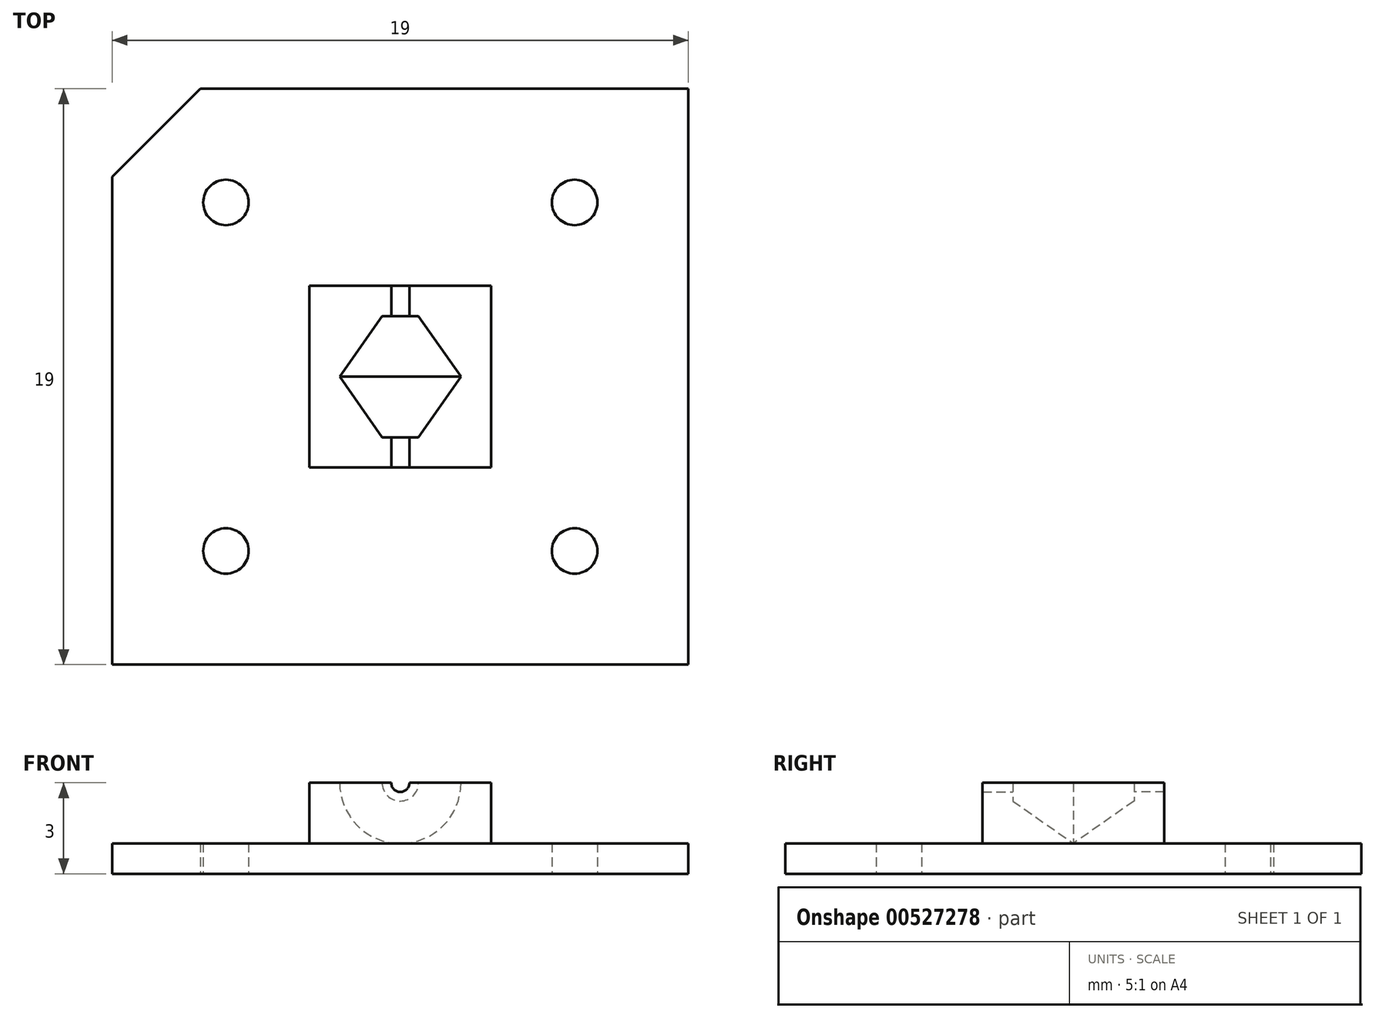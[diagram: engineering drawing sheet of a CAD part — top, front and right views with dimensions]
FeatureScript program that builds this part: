
annotation { "Feature Type Name" : "Feature", "Feature Type Description" : "" }
export const myFeature = defineFeature(function(context is Context, id is Id, definition is map)
    precondition{}
    {
        {
            var Q0;
            Q0=qCreatedBy(makeId("Top.planeOp"),FACE);
            var sketch = newSketch(context, id + "F0", { "sketchPlane" : qUnion([Q0])});
            skLineSegment(sketch, "E0.bottom", {"start": v(-2, 2) * mm, "end": v(2, 2) * mm});
            skLineSegment(sketch, "E0.top", {"start": v(-2, -2) * mm, "end": v(2, -2) * mm});
            skLineSegment(sketch, "E0.left", {"start": v(-2, 2) * mm, "end": v(-2, -2) * mm});
            skLineSegment(sketch, "E0.right", {"start": v(2, 2) * mm, "end": v(2, -2) * mm});
            skPoint(sketch, "E0.middle", {"position": v(0, 0) * mm});
            skLineSegment(sketch, "E1", {"start": v(0.6, 2) * mm, "end": v(2, 0) * mm});
            skLineSegment(sketch, "E2.MirrorCS", {"start": v(0.6, -2) * mm, "end": v(2, 0) * mm});
            skLineSegment(sketch, "E3.MirrorCS", {"start": v(-0.6, 2) * mm, "end": v(-2, 0) * mm});
            skLineSegment(sketch, "E4.MirrorCS", {"start": v(-0.6, -2) * mm, "end": v(-2, 0) * mm});
            skLineSegment(sketch, "E5", {"start": v(-0.6, -2) * mm, "end": v(-0.6, 2) * mm});
            skLineSegment(sketch, "E6.MirrorCS", {"start": v(0.6, -2) * mm, "end": v(0.6, 2) * mm});
            skLineSegment(sketch, "E7", {"start": v(0, 2) * mm, "end": v(0, -2) * mm});
            skCircle(sketch, "E8", {"center": v(-5.75, 5.75) * mm, "radius": 0.75 * mm});
            skCircle(sketch, "E9.MirrorC", {"center": v(5.75, 5.75) * mm, "radius": 0.75 * mm});
            skCircle(sketch, "E10.MirrorC", {"center": v(5.75, -5.75) * mm, "radius": 0.75 * mm});
            skCircle(sketch, "E11.MirrorC", {"center": v(-5.75, -5.75) * mm, "radius": 0.75 * mm});
            skLineSegment(sketch, "E12.bottom", {"start": v(-9.5, 9.5) * mm, "end": v(9.5, 9.5) * mm});
            skLineSegment(sketch, "E12.top", {"start": v(-9.5, -9.5) * mm, "end": v(9.5, -9.5) * mm});
            skLineSegment(sketch, "E12.left", {"start": v(-9.5, 9.5) * mm, "end": v(-9.5, -9.5) * mm});
            skLineSegment(sketch, "E12.right", {"start": v(9.5, 9.5) * mm, "end": v(9.5, -9.5) * mm});
            skLineSegment(sketch, "E13", {"start": v(0.3, 2) * mm, "end": v(0.3, -2) * mm});
            skLineSegment(sketch, "E14.MirrorCS", {"start": v(-0.3, 2) * mm, "end": v(-0.3, -2) * mm});
            skLineSegment(sketch, "E15", {"start": v(-6.6, 9.5) * mm, "end": v(-9.5, 6.6) * mm});
            skSolve(sketch);
        }
        {
            var Q0;
            Q0=qCreatedBy(makeId("Front.planeOp"),FACE);
            var sketch = newSketch(context, id + "F1", { "sketchPlane" : qUnion([Q0])});
            skLineSegment(sketch, "E16.bottom", {"start": v(0, 0) * mm, "end": v(2, 0) * mm});
            skLineSegment(sketch, "E16.top", {"start": v(0, 3) * mm, "end": v(2, 3) * mm});
            skLineSegment(sketch, "E16.left", {"start": v(0, 0) * mm, "end": v(0, 3) * mm});
            skLineSegment(sketch, "E16.right", {"start": v(2, 0) * mm, "end": v(2, 3) * mm});
            skCircle(sketch, "E17", {"center": v(0, 3) * mm, "radius": 0.6 * mm});
            skCircle(sketch, "E18", {"center": v(0, 3) * mm, "radius": 0.3 * mm});
            skLineSegment(sketch, "E19.bottom", {"start": v(0, 3) * mm, "end": v(-2, 3) * mm});
            skLineSegment(sketch, "E19.top", {"start": v(0, 0) * mm, "end": v(-2, 0) * mm});
            skLineSegment(sketch, "E19.left", {"start": v(0, 3) * mm, "end": v(0, 0) * mm});
            skLineSegment(sketch, "E19.right", {"start": v(-2, 3) * mm, "end": v(-2, 0) * mm});
            skLineSegment(sketch, "E20.top", {"start": v(0, 1) * mm, "end": v(2, 1) * mm});
            skLineSegment(sketch, "E20.left", {"start": v(0, 0) * mm, "end": v(0, 1) * mm});
            skLineSegment(sketch, "E21.MirrorCS", {"start": v(0, 1) * mm, "end": v(-2, 1) * mm});
            skSolve(sketch);
        }
        {
            var Q0;
            {var subQ3=sQuery(id+"F0.wireOp",EDGE,"E4.MirrorCS");Q0=makeQuery(id+"F0.imprint","IMPRINT",FACE,{"disambiguationData":[TD([[makeQuery(id+"F0.imprint","IMPRINT",EDGE,{"derivedFrom":subQ3}),1.0]])]});}
            var Q1;
            {var subQ3=sQuery(id+"F0.wireOp",EDGE,"E3.MirrorCS");Q1=makeQuery(id+"F0.imprint","IMPRINT",FACE,{"disambiguationData":[TD([[makeQuery(id+"F0.imprint","IMPRINT",EDGE,{"derivedFrom":subQ3}),-1.0]])]});}
            var Q2;
            {var subQ3=sQuery(id+"F0.wireOp",EDGE,"E1");Q2=makeQuery(id+"F0.imprint","IMPRINT",FACE,{"disambiguationData":[TD([[makeQuery(id+"F0.imprint","IMPRINT",EDGE,{"derivedFrom":subQ3}),1.0]])]});}
            var Q3;
            {var subQ3=sQuery(id+"F0.wireOp",EDGE,"E2.MirrorCS");Q3=makeQuery(id+"F0.imprint","IMPRINT",FACE,{"disambiguationData":[TD([[makeQuery(id+"F0.imprint","IMPRINT",EDGE,{"derivedFrom":subQ3}),-1.0]])]});}
            extrude(context, id + "F2", {"entities" : qUnion([Q0, Q1, Q2, Q3]), "depth" : 3 * mm, "offsetDistance" : 25 * mm});
        }
        {
            var Q0;
            Q0=makeQuery(id+"F0.imprint","IMPRINT",FACE,{"disambiguationData":[TD([[makeQuery(id+"F0.imprint","IMPRINT",EDGE,{"derivedFrom":sQuery(id+"F0.wireOp",EDGE,"E3.MirrorCS")}),1.0]])]});
            var Q1;
            {var subQ0=sQuery(id+"F0.wireOp",EDGE,"E5");Q1=makeQuery(id+"F0.imprint","IMPRINT",FACE,{"disambiguationData":[TD([[makeQuery(id+"F0.imprint","IMPRINT",EDGE,{"derivedFrom":subQ0}),-1.0]])]});}
            var Q2;
            {var subQ0=sQuery(id+"F0.wireOp",EDGE,"E7");Q2=makeQuery(id+"F0.imprint","IMPRINT",FACE,{"disambiguationData":[TD([[makeQuery(id+"F0.imprint","IMPRINT",EDGE,{"derivedFrom":subQ0}),-1.0]])]});}
            extrude(context, id + "F3", {"entities" : qUnion([Q0, Q1, Q2]), "depth" : 3 * mm, "offsetDistance" : 25 * mm});
        }
        {
            var Q0;
            {var subQ0=sQuery(id+"F0.wireOp",EDGE,"E6.MirrorCS");Q0=makeQuery(id+"F0.imprint","IMPRINT",FACE,{"disambiguationData":[TD([[makeQuery(id+"F0.imprint","IMPRINT",EDGE,{"derivedFrom":subQ0}),1.0]])]});}
            var Q1;
            Q1=makeQuery(id+"F0.imprint","IMPRINT",FACE,{"disambiguationData":[TD([[makeQuery(id+"F0.imprint","IMPRINT",EDGE,{"derivedFrom":sQuery(id+"F0.wireOp",EDGE,"E1")}),-1.0]])]});
            var Q2;
            {var subQ0=sQuery(id+"F0.wireOp",EDGE,"E7");Q2=makeQuery(id+"F0.imprint","IMPRINT",FACE,{"disambiguationData":[TD([[makeQuery(id+"F0.imprint","IMPRINT",EDGE,{"derivedFrom":subQ0}),1.0]])]});}
            extrude(context, id + "F4", {"entities" : qUnion([Q0, Q1, Q2]), "depth" : 3 * mm, "offsetDistance" : 25 * mm});
        }
        {
            var Q0;
            Q0=makeQuery(id+"F4.opExtrude","CAP_FACE",FACE,{"disambiguationData":[OSD([sQuery(id+"F0.wireOp",EDGE,"E0.bottom"),sQuery(id+"F0.wireOp",EDGE,"E0.top"),sQuery(id+"F0.wireOp",EDGE,"E1"),sQuery(id+"F0.wireOp",EDGE,"E2.MirrorCS"),sQuery(id+"F0.wireOp",EDGE,"E7")])],"isStart":false});
            var Q1;
            Q1=makeQuery(id+"F3.opExtrude","CAP_EDGE",EDGE,{"disambiguationData":[OSD([sQuery(id+"F0.wireOp",EDGE,"E7")])],"isStart":false});
            revolve(context, id + "F5", {"operationType" : NewBodyOperationType.REMOVE, "entities" : qUnion([Q0]), "axis" : qUnion([Q1]), "revolveType" : RevolveType.FULL, "oppositeDirection" : true});
        }
        {
            var Q0;
            Q0=makeQuery(id+"F2.opExtrude","SWEPT_BODY",BODY,{"disambiguationData":[OSD([sQuery(id+"F0.wireOp",EDGE,"E0.bottom"),sQuery(id+"F0.wireOp",EDGE,"E0.left"),sQuery(id+"F0.wireOp",EDGE,"E3.MirrorCS")])]});
            var Q1;
            Q1=makeQuery(id+"F2.opExtrude","SWEPT_BODY",BODY,{"disambiguationData":[OSD([sQuery(id+"F0.wireOp",EDGE,"E0.top"),sQuery(id+"F0.wireOp",EDGE,"E0.left"),sQuery(id+"F0.wireOp",EDGE,"E4.MirrorCS")])]});
            var Q2;
            Q2=makeQuery(id+"F3.opExtrude","SWEPT_BODY",BODY,{"disambiguationData":[OSD([sQuery(id+"F0.wireOp",EDGE,"E0.bottom"),sQuery(id+"F0.wireOp",EDGE,"E0.top"),sQuery(id+"F0.wireOp",EDGE,"E3.MirrorCS"),sQuery(id+"F0.wireOp",EDGE,"E4.MirrorCS"),sQuery(id+"F0.wireOp",EDGE,"E7")])]});
            var Q3;
            Q3=makeQuery(id+"F4.opExtrude","SWEPT_BODY",BODY,{"disambiguationData":[OSD([sQuery(id+"F0.wireOp",EDGE,"E0.bottom"),sQuery(id+"F0.wireOp",EDGE,"E0.top"),sQuery(id+"F0.wireOp",EDGE,"E1"),sQuery(id+"F0.wireOp",EDGE,"E2.MirrorCS"),sQuery(id+"F0.wireOp",EDGE,"E7")])]});
            var Q4;
            Q4=makeQuery(id+"F2.opExtrude","SWEPT_BODY",BODY,{"disambiguationData":[OSD([sQuery(id+"F0.wireOp",EDGE,"E0.bottom"),sQuery(id+"F0.wireOp",EDGE,"E0.right"),sQuery(id+"F0.wireOp",EDGE,"E1")])]});
            var Q5;
            Q5=makeQuery(id+"F2.opExtrude","SWEPT_BODY",BODY,{"disambiguationData":[OSD([sQuery(id+"F0.wireOp",EDGE,"E0.top"),sQuery(id+"F0.wireOp",EDGE,"E0.right"),sQuery(id+"F0.wireOp",EDGE,"E2.MirrorCS")])]});
            booleanBodies(context, id + "F6", {"operationType" : BooleanOperationType.UNION, "tools" : qUnion([Q0, Q1, Q2, Q3, Q4, Q5])});
        }
        {
            var Q0;
            {var subQ0=sQuery(id+"F1.wireOp",EDGE,"E19.bottom");var subQ1=sQuery(id+"F1.wireOp",EDGE,"E17");var subQ2=makeQuery(id+"F1.imprint","INTERSECT",VERTEX,{"derivedFrom":[subQ1,subQ0]});Q0=makeQuery(id+"F1.imprint","IMPRINT",FACE,{"disambiguationData":[TD([[makeQuery(id+"F1.imprint","IMPRINT",EDGE,{"disambiguationData":[TD([[subQ2,-1.0]])],"derivedFrom":subQ1}),1.0]])]});}
            var Q1;
            {var subQ0=sQuery(id+"F1.wireOp",EDGE,"E17");var subQ1=sQuery(id+"F1.wireOp",EDGE,"E16.top");var subQ2=makeQuery(id+"F1.imprint","INTERSECT",VERTEX,{"derivedFrom":[subQ1,subQ0]});Q1=makeQuery(id+"F1.imprint","IMPRINT",FACE,{"disambiguationData":[TD([[makeQuery(id+"F1.imprint","IMPRINT",EDGE,{"disambiguationData":[TD([[subQ2,1.0]])],"derivedFrom":subQ1}),-1.0]])]});}
            extrude(context, id + "F7", {"entities" : qUnion([Q0, Q1]), "depth" : 3 * mm, "offsetDistance" : 25 * mm});
        }
        {
            var Q0;
            {var subQ0=sQuery(id+"F1.wireOp",EDGE,"E19.bottom");var subQ1=sQuery(id+"F1.wireOp",EDGE,"E17");var subQ2=makeQuery(id+"F1.imprint","INTERSECT",VERTEX,{"derivedFrom":[subQ1,subQ0]});Q0=makeQuery(id+"F1.imprint","IMPRINT",FACE,{"disambiguationData":[TD([[makeQuery(id+"F1.imprint","IMPRINT",EDGE,{"disambiguationData":[TD([[subQ2,-1.0]])],"derivedFrom":subQ1}),1.0]])]});}
            var Q1;
            {var subQ0=sQuery(id+"F1.wireOp",EDGE,"E17");var subQ1=sQuery(id+"F1.wireOp",EDGE,"E16.top");var subQ2=makeQuery(id+"F1.imprint","INTERSECT",VERTEX,{"derivedFrom":[subQ1,subQ0]});Q1=makeQuery(id+"F1.imprint","IMPRINT",FACE,{"disambiguationData":[TD([[makeQuery(id+"F1.imprint","IMPRINT",EDGE,{"disambiguationData":[TD([[subQ2,1.0]])],"derivedFrom":subQ1}),-1.0]])]});}
            extrude(context, id + "F8", {"entities" : qUnion([Q0, Q1]), "operationType" : NewBodyOperationType.REMOVE, "depth" : 2 * mm, "offsetDistance" : 25 * mm});
        }
        {
            var Q0;
            {var subQ0=sQuery(id+"F0.wireOp",EDGE,"E0.top");Q0=makeQuery(id+"F6.opBoolean","MERGE",FACE,{"derivedFrom":[makeQuery(id+"F2.opExtrude","SWEPT_FACE",FACE,{"disambiguationData":[OSD([subQ0]),TDD([makeQuery(id+"F0.imprint","IMPRINT",EDGE,{"disambiguationData":[TD([[makeQuery(id+"F0.imprint","INTERSECT",VERTEX,{"derivedFrom":[subQ0,sQuery(id+"F0.wireOp",EDGE,"E0.left")]}),-1.0]])],"derivedFrom":subQ0})])]}),makeQuery(id+"F2.opExtrude","SWEPT_FACE",FACE,{"disambiguationData":[OSD([subQ0]),TDD([makeQuery(id+"F0.imprint","IMPRINT",EDGE,{"disambiguationData":[TD([[makeQuery(id+"F0.imprint","INTERSECT",VERTEX,{"derivedFrom":[subQ0,sQuery(id+"F0.wireOp",EDGE,"E0.right")]}),1.0]])],"derivedFrom":subQ0})])]}),makeQuery(id+"F3.opExtrude","SWEPT_FACE",FACE,{"disambiguationData":[OSD([subQ0])]}),makeQuery(id+"F4.opExtrude","SWEPT_FACE",FACE,{"disambiguationData":[OSD([subQ0])]})]});}
            extrude(context, id + "F9", {"entities" : qUnion([Q0]), "depth" : 1 * mm, "offsetDistance" : 25 * mm});
        }
        {
            var Q0;
            Q0=makeQuery(id+"F7.opExtrude","SWEPT_BODY",BODY,{"disambiguationData":[OSD([sQuery(id+"F1.wireOp",EDGE,"E16.top"),sQuery(id+"F1.wireOp",EDGE,"E17"),sQuery(id+"F1.wireOp",EDGE,"E18"),sQuery(id+"F1.wireOp",EDGE,"E19.bottom")])]});
            var Q1;
            Q1=makeQuery(id+"F2.opExtrude","SWEPT_BODY",BODY,{"disambiguationData":[OSD([sQuery(id+"F0.wireOp",EDGE,"E0.bottom"),sQuery(id+"F0.wireOp",EDGE,"E0.left"),sQuery(id+"F0.wireOp",EDGE,"E3.MirrorCS")])]});
            var Q2;
            Q2=makeQuery(id+"F9.opExtrude","SWEPT_BODY",BODY,{"disambiguationData":[OSD([sQuery(id+"F0.wireOp",EDGE,"E0.top")])]});
            booleanBodies(context, id + "F10", {"operationType" : BooleanOperationType.UNION, "tools" : qUnion([Q0, Q1, Q2])});
        }
        {
            var Q0;
            {var subQ0=sQuery(id+"F1.wireOp",EDGE,"E17");var subQ1=sQuery(id+"F1.wireOp",EDGE,"E16.top");var subQ2=makeQuery(id+"F1.imprint","INTERSECT",VERTEX,{"derivedFrom":[subQ1,subQ0]});Q0=makeQuery(id+"F1.imprint","IMPRINT",FACE,{"disambiguationData":[TD([[makeQuery(id+"F1.imprint","IMPRINT",EDGE,{"disambiguationData":[TD([[subQ2,1.0]])],"derivedFrom":subQ1}),-1.0]])]});}
            var Q1;
            {var subQ0=sQuery(id+"F1.wireOp",EDGE,"E19.bottom");var subQ1=sQuery(id+"F1.wireOp",EDGE,"E17");var subQ2=makeQuery(id+"F1.imprint","INTERSECT",VERTEX,{"derivedFrom":[subQ1,subQ0]});Q1=makeQuery(id+"F1.imprint","IMPRINT",FACE,{"disambiguationData":[TD([[makeQuery(id+"F1.imprint","IMPRINT",EDGE,{"disambiguationData":[TD([[subQ2,-1.0]])],"derivedFrom":subQ1}),1.0]])]});}
            extrude(context, id + "F11", {"entities" : qUnion([Q0, Q1]), "oppositeDirection" : true, "depth" : 3 * mm, "offsetDistance" : 25 * mm});
        }
        {
            var Q0;
            {var subQ0=sQuery(id+"F1.wireOp",EDGE,"E17");var subQ1=sQuery(id+"F1.wireOp",EDGE,"E16.top");var subQ2=makeQuery(id+"F1.imprint","INTERSECT",VERTEX,{"derivedFrom":[subQ1,subQ0]});Q0=makeQuery(id+"F1.imprint","IMPRINT",FACE,{"disambiguationData":[TD([[makeQuery(id+"F1.imprint","IMPRINT",EDGE,{"disambiguationData":[TD([[subQ2,1.0]])],"derivedFrom":subQ1}),-1.0]])]});}
            var Q1;
            {var subQ0=sQuery(id+"F1.wireOp",EDGE,"E19.bottom");var subQ1=sQuery(id+"F1.wireOp",EDGE,"E17");var subQ2=makeQuery(id+"F1.imprint","INTERSECT",VERTEX,{"derivedFrom":[subQ1,subQ0]});Q1=makeQuery(id+"F1.imprint","IMPRINT",FACE,{"disambiguationData":[TD([[makeQuery(id+"F1.imprint","IMPRINT",EDGE,{"disambiguationData":[TD([[subQ2,-1.0]])],"derivedFrom":subQ1}),1.0]])]});}
            extrude(context, id + "F12", {"entities" : qUnion([Q0, Q1]), "operationType" : NewBodyOperationType.REMOVE, "oppositeDirection" : true, "depth" : 2 * mm, "offsetDistance" : 25 * mm});
        }
        {
            var Q0;
            {var subQ0=sQuery(id+"F0.wireOp",EDGE,"E0.bottom");Q0=makeQuery(id+"F6.opBoolean","MERGE",FACE,{"derivedFrom":[makeQuery(id+"F2.opExtrude","SWEPT_FACE",FACE,{"disambiguationData":[OSD([subQ0]),TDD([makeQuery(id+"F0.imprint","IMPRINT",EDGE,{"disambiguationData":[TD([[makeQuery(id+"F0.imprint","INTERSECT",VERTEX,{"derivedFrom":[subQ0,sQuery(id+"F0.wireOp",EDGE,"E0.left")]}),-1.0]])],"derivedFrom":subQ0})])]}),makeQuery(id+"F2.opExtrude","SWEPT_FACE",FACE,{"disambiguationData":[OSD([subQ0]),TDD([makeQuery(id+"F0.imprint","IMPRINT",EDGE,{"disambiguationData":[TD([[makeQuery(id+"F0.imprint","INTERSECT",VERTEX,{"derivedFrom":[subQ0,sQuery(id+"F0.wireOp",EDGE,"E0.right")]}),1.0]])],"derivedFrom":subQ0})])]}),makeQuery(id+"F3.opExtrude","SWEPT_FACE",FACE,{"disambiguationData":[OSD([subQ0])]}),makeQuery(id+"F4.opExtrude","SWEPT_FACE",FACE,{"disambiguationData":[OSD([subQ0])]})]});}
            extrude(context, id + "F13", {"entities" : qUnion([Q0]), "depth" : 1 * mm, "offsetDistance" : 25 * mm});
        }
        {
            var Q0;
            Q0=makeQuery(id+"F11.opExtrude","SWEPT_BODY",BODY,{"disambiguationData":[OSD([sQuery(id+"F1.wireOp",EDGE,"E16.top"),sQuery(id+"F1.wireOp",EDGE,"E17"),sQuery(id+"F1.wireOp",EDGE,"E18"),sQuery(id+"F1.wireOp",EDGE,"E19.bottom")])]});
            var Q1;
            Q1=makeQuery(id+"F13.opExtrude","SWEPT_BODY",BODY,{"disambiguationData":[OSD([sQuery(id+"F0.wireOp",EDGE,"E0.bottom")])]});
            var Q2;
            Q2=makeQuery(id+"F7.opExtrude","SWEPT_BODY",BODY,{"disambiguationData":[OSD([sQuery(id+"F1.wireOp",EDGE,"E16.top"),sQuery(id+"F1.wireOp",EDGE,"E17"),sQuery(id+"F1.wireOp",EDGE,"E18"),sQuery(id+"F1.wireOp",EDGE,"E19.bottom")])]});
            booleanBodies(context, id + "F14", {"operationType" : BooleanOperationType.UNION, "tools" : qUnion([Q0, Q1, Q2])});
        }
        {
            var Q0;
            {var subQ0=sQuery(id+"F0.wireOp",EDGE,"E0.right");var subQ1=sQuery(id+"F0.wireOp",EDGE,"E0.bottom");var subQ2=sQuery(id+"F0.wireOp",EDGE,"E0.top");Q0=makeQuery(id+"F14.opBoolean","MERGE",FACE,{"derivedFrom":[makeQuery(id+"F10.opBoolean","MERGE",FACE,{"derivedFrom":[makeQuery(id+"F6.opBoolean","MERGE",FACE,{"derivedFrom":[makeQuery(id+"F2.opExtrude","SWEPT_FACE",FACE,{"disambiguationData":[OSD([subQ0]),TDD([makeQuery(id+"F0.imprint","IMPRINT",EDGE,{"disambiguationData":[TD([[makeQuery(id+"F0.imprint","INTERSECT",VERTEX,{"derivedFrom":[subQ1,subQ0]}),-1.0]])],"derivedFrom":subQ0})])]}),makeQuery(id+"F2.opExtrude","SWEPT_FACE",FACE,{"disambiguationData":[OSD([subQ0]),TDD([makeQuery(id+"F0.imprint","IMPRINT",EDGE,{"disambiguationData":[TD([[makeQuery(id+"F0.imprint","INTERSECT",VERTEX,{"derivedFrom":[subQ2,subQ0]}),1.0]])],"derivedFrom":subQ0})])]})]}),makeQuery(id+"F9.opExtrude","SWEPT_FACE",FACE,{"disambiguationData":[OSD([subQ2,subQ0])]})]}),makeQuery(id+"F13.opExtrude","SWEPT_FACE",FACE,{"disambiguationData":[OSD([subQ1,subQ0])]})]});}
            extrude(context, id + "F15", {"entities" : qUnion([Q0]), "operationType" : NewBodyOperationType.ADD, "depth" : 1 * mm, "offsetDistance" : 25 * mm});
        }
        {
            var Q0;
            {var subQ0=sQuery(id+"F0.wireOp",EDGE,"E0.left");var subQ1=sQuery(id+"F0.wireOp",EDGE,"E0.bottom");var subQ2=sQuery(id+"F0.wireOp",EDGE,"E0.top");Q0=makeQuery(id+"F14.opBoolean","MERGE",FACE,{"derivedFrom":[makeQuery(id+"F10.opBoolean","MERGE",FACE,{"derivedFrom":[makeQuery(id+"F6.opBoolean","MERGE",FACE,{"derivedFrom":[makeQuery(id+"F2.opExtrude","SWEPT_FACE",FACE,{"disambiguationData":[OSD([subQ0]),TDD([makeQuery(id+"F0.imprint","IMPRINT",EDGE,{"disambiguationData":[TD([[makeQuery(id+"F0.imprint","INTERSECT",VERTEX,{"derivedFrom":[subQ1,subQ0]}),-1.0]])],"derivedFrom":subQ0})])]}),makeQuery(id+"F2.opExtrude","SWEPT_FACE",FACE,{"disambiguationData":[OSD([subQ0]),TDD([makeQuery(id+"F0.imprint","IMPRINT",EDGE,{"disambiguationData":[TD([[makeQuery(id+"F0.imprint","INTERSECT",VERTEX,{"derivedFrom":[subQ2,subQ0]}),1.0]])],"derivedFrom":subQ0})])]})]}),makeQuery(id+"F9.opExtrude","SWEPT_FACE",FACE,{"disambiguationData":[OSD([subQ2,subQ0])]})]}),makeQuery(id+"F13.opExtrude","SWEPT_FACE",FACE,{"disambiguationData":[OSD([subQ1,subQ0])]})]});}
            extrude(context, id + "F16", {"entities" : qUnion([Q0]), "operationType" : NewBodyOperationType.ADD, "depth" : 1 * mm, "offsetDistance" : 25 * mm});
        }
        {
            var Q0;
            Q0=makeQuery(id+"F0.imprint","IMPRINT",FACE,{"disambiguationData":[TD([[makeQuery(id+"F0.imprint","IMPRINT",EDGE,{"derivedFrom":sQuery(id+"F0.wireOp",EDGE,"E8")}),-1.0]])]});
            extrude(context, id + "F17", {"entities" : qUnion([Q0]), "operationType" : NewBodyOperationType.ADD, "depth" : 1 * mm, "offsetDistance" : 25 * mm});
        }
    });
